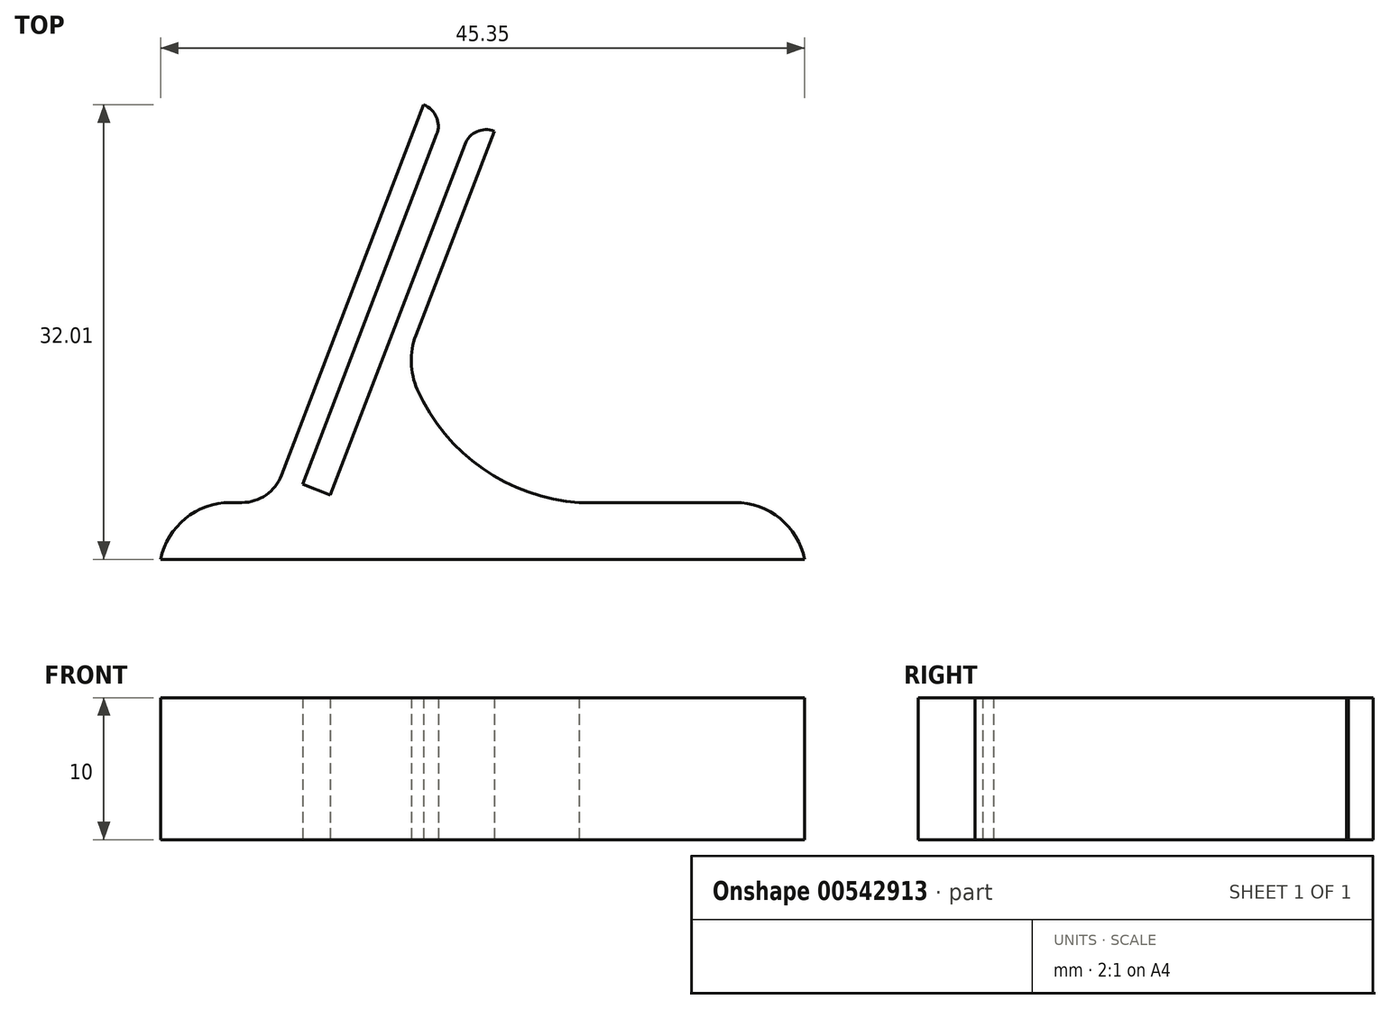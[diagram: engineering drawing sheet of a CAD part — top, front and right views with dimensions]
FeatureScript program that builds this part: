
annotation { "Feature Type Name" : "Feature", "Feature Type Description" : "" }
export const myFeature = defineFeature(function(context is Context, id is Id, definition is map)
    precondition{}
    {
        {
            var Q0;
            Q0=qCreatedBy(makeId("Top.planeOp"),FACE);
            var sketch = newSketch(context, id + "F0", { "sketchPlane" : qUnion([Q0])});
            skLineSegment(sketch, "E0.bottom", {"start": v(-7.78, 0) * mm, "end": v(37.57, 0) * mm});
            skLineSegment(sketch, "E0.top", {"start": v(-7.78, 4) * mm, "end": v(0, 4) * mm});
            skLineSegment(sketch, "E0.right", {"start": v(37.57, 0) * mm, "end": v(37.57, 4) * mm});
            skLineSegment(sketch, "E1", {"start": v(0, 4) * mm, "end": v(10.74, 32.01) * mm});
            skLineSegment(sketch, "E2", {"start": v(10.74, 32.01) * mm, "end": v(12.24, 31.44) * mm});
            skLineSegment(sketch, "E3", {"start": v(12.24, 31.44) * mm, "end": v(2.21, 5.3) * mm});
            skLineSegment(sketch, "E4", {"start": v(2.21, 5.3) * mm, "end": v(4.17, 4.54) * mm});
            skLineSegment(sketch, "E5", {"start": v(4.17, 4.54) * mm, "end": v(14.22, 30.73) * mm});
            skLineSegment(sketch, "E6", {"start": v(14.22, 30.73) * mm, "end": v(15.7, 30.16) * mm});
            skLineSegment(sketch, "E7", {"start": v(15.7, 30.16) * mm, "end": v(9.55, 14.1) * mm});
            skArc(sketch, "E8", {"start": v(9.55, 14.1) * mm, "mid": v(13.99, 7.08) * mm, "end": v(21.7, 4) * mm});
            skLineSegment(sketch, "E9", {"start": v(-7.78, 4) * mm, "end": v(-7.78, 0) * mm});
            skPoint(sketch, "E0.left.start.orphan", {"position": v(-22.43, 0) * mm});
            skLineSegment(sketch, "E10.trimOffspring", {"start": v(21.7, 4) * mm, "end": v(37.57, 4) * mm});
            skSolve(sketch);
        }
        {
            var Q0;
            Q0=makeQuery(id+"F0.imprint","IMPRINT",FACE,{"disambiguationData":[TD([[makeQuery(id+"F0.imprint","IMPRINT",EDGE,{"derivedFrom":sQuery(id+"F0.wireOp",EDGE,"E0.bottom")}),1.0]])]});
            extrude(context, id + "F1", {"entities" : qUnion([Q0]), "depth" : 10 * mm, "offsetDistance" : 25 * mm});
        }
        {
            var Q0;
            Q0=makeQuery(id+"F1.opExtrude","SWEPT_EDGE",EDGE,{"disambiguationData":[OSD([sQuery(id+"F0.wireOp",EDGE,"E0.top"),sQuery(id+"F0.wireOp",EDGE,"E9")])]});
            var Q1;
            Q1=makeQuery(id+"F1.opExtrude","SWEPT_EDGE",EDGE,{"disambiguationData":[OSD([sQuery(id+"F0.wireOp",EDGE,"E0.right"),sQuery(id+"F0.wireOp",EDGE,"E10.trimOffspring")])]});
            var Q2;
            Q2=makeQuery(id+"F1.opExtrude","SWEPT_EDGE",EDGE,{"disambiguationData":[OSD([sQuery(id+"F0.wireOp",EDGE,"E7"),sQuery(id+"F0.wireOp",EDGE,"E8")])]});
            fillet(context, id + "F2", {"entities" : qUnion([Q0, Q1, Q2]), "radius" : 5 * mm, "tangentPropagation" : true, "allowEdgeOverflow" : false});
        }
        {
            var Q0;
            Q0=makeQuery(id+"F1.opExtrude","SWEPT_EDGE",EDGE,{"disambiguationData":[OSD([sQuery(id+"F0.wireOp",EDGE,"E0.top"),sQuery(id+"F0.wireOp",EDGE,"E1")])]});
            fillet(context, id + "F3", {"entities" : qUnion([Q0]), "radius" : 3 * mm, "tangentPropagation" : true, "allowEdgeOverflow" : false});
        }
        {
            var Q0;
            Q0=makeQuery(id+"F1.opExtrude","SWEPT_EDGE",EDGE,{"disambiguationData":[OSD([sQuery(id+"F0.wireOp",EDGE,"E2"),sQuery(id+"F0.wireOp",EDGE,"E3")])]});
            var Q1;
            Q1=makeQuery(id+"F1.opExtrude","SWEPT_EDGE",EDGE,{"disambiguationData":[OSD([sQuery(id+"F0.wireOp",EDGE,"E5"),sQuery(id+"F0.wireOp",EDGE,"E6")])]});
            fillet(context, id + "F4", {"entities" : qUnion([Q0, Q1]), "radius" : 1.6 * mm, "tangentPropagation" : true, "allowEdgeOverflow" : false});
        }
    });
